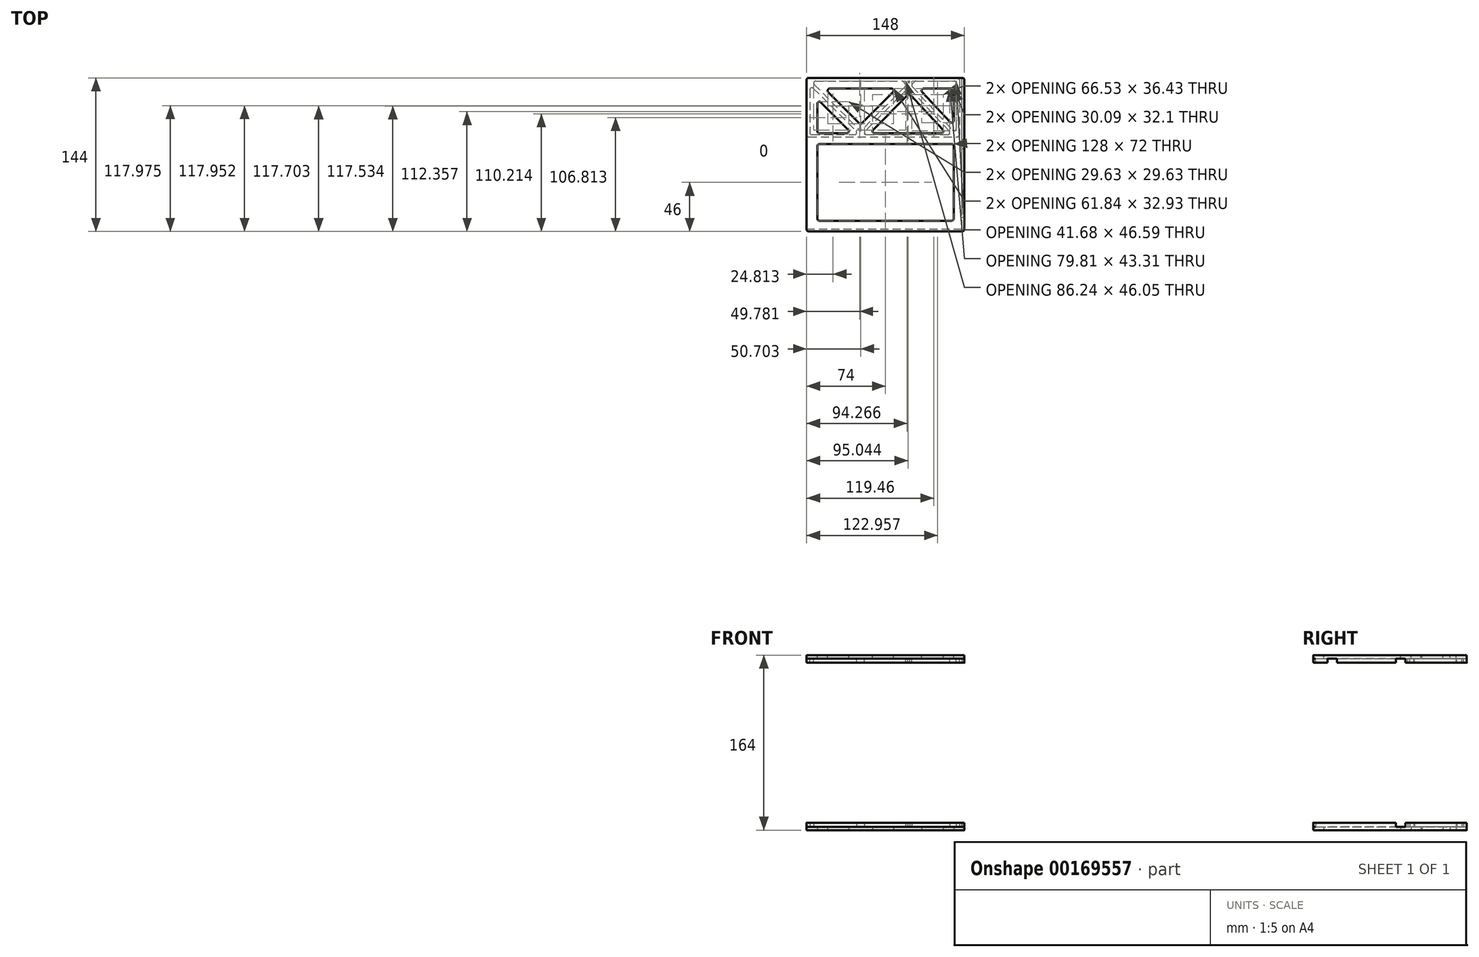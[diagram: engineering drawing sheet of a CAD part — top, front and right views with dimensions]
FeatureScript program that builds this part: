
annotation { "Feature Type Name" : "Feature", "Feature Type Description" : "" }
export const myFeature = defineFeature(function(context is Context, id is Id, definition is map)
    precondition{}
    {
        {
            var Q0;
            Q0=qCreatedBy(makeId("Top.planeOp"),FACE);
            var sketch = newSketch(context, id + "F0", { "sketchPlane" : qUnion([Q0])});
            skLineSegment(sketch, "E0.bottom", {"start": v(72, -72) * mm, "end": v(-72, -72) * mm});
            skLineSegment(sketch, "E0.top", {"start": v(72, 72) * mm, "end": v(-72, 72) * mm});
            skLineSegment(sketch, "E0.left", {"start": v(74, -70) * mm, "end": v(74, 70) * mm});
            skLineSegment(sketch, "E0.right", {"start": v(-74, -70) * mm, "end": v(-74, 70) * mm});
            skPoint(sketch, "E0.middle", {"position": v(0, 0) * mm});
            skLineSegment(sketch, "E1", {"start": v(-64, 8) * mm, "end": v(-64, -60) * mm});
            skLineSegment(sketch, "E2", {"start": v(-62, 20) * mm, "end": v(-36.36, 20) * mm});
            skPoint(sketch, "E3.end.orphan", {"position": v(-74, 0) * mm});
            skLineSegment(sketch, "E4", {"start": v(64, 60) * mm, "end": v(64, 31.9) * mm});
            skLineSegment(sketch, "E5", {"start": v(-71, -69) * mm, "end": v(71, -69) * mm, "construction": true});
            skLineSegment(sketch, "E6", {"start": v(71, -69) * mm, "end": v(71, 68) * mm, "construction": true});
            skLineSegment(sketch, "E7", {"start": v(71, 68) * mm, "end": v(69, 68) * mm, "construction": true});
            skLineSegment(sketch, "E8", {"start": v(69, 68) * mm, "end": v(69, 17) * mm, "construction": true});
            skLineSegment(sketch, "E9", {"start": v(69, 17) * mm, "end": v(-71, 17) * mm, "construction": true});
            skLineSegment(sketch, "E10", {"start": v(-71, 17) * mm, "end": v(-71, -69) * mm, "construction": true});
            skLineSegment(sketch, "E11.trimOffspring", {"start": v(-62, 10) * mm, "end": v(62, 10) * mm});
            skLineSegment(sketch, "E12.trimOffspring", {"start": v(64, 8) * mm, "end": v(64, -60) * mm});
            skLineSegment(sketch, "E13.trimOffspring", {"start": v(-62, -62) * mm, "end": v(62, -62) * mm});
            skLineSegment(sketch, "E14", {"start": v(-60.59, 49.05) * mm, "end": v(-34.95, 23.41) * mm});
            skLineSegment(sketch, "E15", {"start": v(-11.64, 23.41) * mm, "end": v(20.79, 55.84) * mm});
            skLineSegment(sketch, "E16", {"start": v(18.94, 62) * mm, "end": v(19.15, 62) * mm});
            skLineSegment(sketch, "E17", {"start": v(23.67, 55.8) * mm, "end": v(53.79, 23.36) * mm});
            skLineSegment(sketch, "E18", {"start": v(56.9, 20) * mm, "end": v(56.9, 20) * mm});
            skLineSegment(sketch, "E19", {"start": v(-53.64, 58.59) * mm, "end": v(-24.71, 29.65) * mm});
            skLineSegment(sketch, "E20", {"start": v(-21.88, 29.65) * mm, "end": v(7.05, 58.59) * mm});
            skLineSegment(sketch, "E21", {"start": v(34.43, 58.64) * mm, "end": v(60.53, 30.54) * mm});
            skLineSegment(sketch, "E22.trimOffspring", {"start": v(-10.23, 20) * mm, "end": v(52.32, 20) * mm});
            skPoint(sketch, "E23.visualSharp", {"position": v(-74, 72) * mm});
            skArc(sketch, "E23.filletArc", {"start": v(-72, 72) * mm, "mid": v(-73.41, 71.41) * mm, "end": v(-74, 70) * mm});
            skPoint(sketch, "E24.visualSharp", {"position": v(74, 72) * mm});
            skArc(sketch, "E24.filletArc", {"start": v(74, 70) * mm, "mid": v(73.41, 71.41) * mm, "end": v(72, 72) * mm});
            skLineSegment(sketch, "E25.trimOffspring", {"start": v(35.9, 62) * mm, "end": v(62, 62) * mm});
            skLineSegment(sketch, "E26.trimOffspring", {"start": v(-52.23, 62) * mm, "end": v(5.64, 62) * mm});
            skLineSegment(sketch, "E27.trimOffspring", {"start": v(-64, 22) * mm, "end": v(-64, 47.64) * mm});
            skPoint(sketch, "E28.visualSharp", {"position": v(-74, -72) * mm});
            skArc(sketch, "E28.filletArc", {"start": v(-74, -70) * mm, "mid": v(-73.41, -71.41) * mm, "end": v(-72, -72) * mm});
            skPoint(sketch, "E29.visualSharp", {"position": v(-64, -62) * mm});
            skArc(sketch, "E29.filletArc", {"start": v(-64, -60) * mm, "mid": v(-63.41, -61.41) * mm, "end": v(-62, -62) * mm});
            skPoint(sketch, "E30.visualSharp", {"position": v(64, -62) * mm});
            skArc(sketch, "E30.filletArc", {"start": v(62, -62) * mm, "mid": v(63.41, -61.41) * mm, "end": v(64, -60) * mm});
            skPoint(sketch, "E31.visualSharp", {"position": v(74, -72) * mm});
            skArc(sketch, "E31.filletArc", {"start": v(72, -72) * mm, "mid": v(73.41, -71.41) * mm, "end": v(74, -70) * mm});
            skPoint(sketch, "E32.visualSharp", {"position": v(64, 26.8) * mm});
            skArc(sketch, "E32.filletArc", {"start": v(60.53, 30.54) * mm, "mid": v(62.73, 30.04) * mm, "end": v(64, 31.9) * mm});
            skPoint(sketch, "E33.visualSharp", {"position": v(56.9, 20) * mm});
            skArc(sketch, "E33.filletArc", {"start": v(52.32, 20) * mm, "mid": v(54.15, 21.2) * mm, "end": v(53.79, 23.36) * mm});
            skPoint(sketch, "E34.visualSharp", {"position": v(64, 10) * mm});
            skArc(sketch, "E34.filletArc", {"start": v(64, 8) * mm, "mid": v(63.41, 9.41) * mm, "end": v(62, 10) * mm});
            skPoint(sketch, "E35.visualSharp", {"position": v(-23.3, 28.24) * mm});
            skArc(sketch, "E35.filletArc", {"start": v(-24.71, 29.65) * mm, "mid": v(-23.3, 29.07) * mm, "end": v(-21.88, 29.65) * mm});
            skPoint(sketch, "E36.visualSharp", {"position": v(-15.06, 20) * mm});
            skArc(sketch, "E36.filletArc", {"start": v(-11.64, 23.41) * mm, "mid": v(-12.08, 21.23) * mm, "end": v(-10.23, 20) * mm});
            skPoint(sketch, "E37.visualSharp", {"position": v(-31.54, 20) * mm});
            skArc(sketch, "E37.filletArc", {"start": v(-36.36, 20) * mm, "mid": v(-34.52, 21.23) * mm, "end": v(-34.95, 23.41) * mm});
            skPoint(sketch, "E38.visualSharp", {"position": v(-64, 20) * mm});
            skArc(sketch, "E38.filletArc", {"start": v(-64, 22) * mm, "mid": v(-63.41, 20.59) * mm, "end": v(-62, 20) * mm});
            skPoint(sketch, "E39.visualSharp", {"position": v(-64, 10) * mm});
            skArc(sketch, "E39.filletArc", {"start": v(-62, 10) * mm, "mid": v(-63.41, 9.41) * mm, "end": v(-64, 8) * mm});
            skPoint(sketch, "E40.visualSharp", {"position": v(-64, 52.46) * mm});
            skArc(sketch, "E40.filletArc", {"start": v(-60.59, 49.05) * mm, "mid": v(-62.77, 49.48) * mm, "end": v(-64, 47.64) * mm});
            skPoint(sketch, "E41.visualSharp", {"position": v(-57.06, 62) * mm});
            skArc(sketch, "E41.filletArc", {"start": v(-52.23, 62) * mm, "mid": v(-54.08, 60.77) * mm, "end": v(-53.64, 58.59) * mm});
            skPoint(sketch, "E42.visualSharp", {"position": v(10.46, 62) * mm});
            skArc(sketch, "E42.filletArc", {"start": v(7.05, 58.59) * mm, "mid": v(7.48, 60.77) * mm, "end": v(5.64, 62) * mm});
            skArc(sketch, "E43.filletArc", {"start": v(23.67, 55.8) * mm, "mid": v(22.24, 56.43) * mm, "end": v(20.79, 55.84) * mm});
            skPoint(sketch, "E44.visualSharp", {"position": v(31.31, 62) * mm});
            skArc(sketch, "E44.filletArc", {"start": v(35.9, 62) * mm, "mid": v(34.07, 60.8) * mm, "end": v(34.43, 58.64) * mm});
            skPoint(sketch, "E45.visualSharp", {"position": v(64, 62) * mm});
            skArc(sketch, "E45.filletArc", {"start": v(64, 60) * mm, "mid": v(63.41, 61.41) * mm, "end": v(62, 62) * mm});
            skSolve(sketch);
        }
        {
            var Q0;
            Q0 = qSketchRegion(id + "F0", true);
            var Q1;
            {var subQ0=sQuery(id+"F0.wireOp",EDGE,"E14");Q1=makeQuery(id+"F0.imprint","IMPRINT",FACE,{"disambiguationData":[TD([[makeQuery(id+"F0.imprint","IMPRINT",EDGE,{"derivedFrom":subQ0}),1.0]])]});}
            extrude(context, id + "F1", {"entities" : qUnion([Q0, Q1]), "depth" : 3 * mm});
        }
        {
            var Q0;
            Q0=makeQuery(id+"F1.opExtrude","CAP_FACE",FACE,{"disambiguationData":[OSD([sQuery(id+"F0.wireOp",EDGE,"E0.bottom"),sQuery(id+"F0.wireOp",EDGE,"E0.top"),sQuery(id+"F0.wireOp",EDGE,"E0.left"),sQuery(id+"F0.wireOp",EDGE,"E0.right"),sQuery(id+"F0.wireOp",EDGE,"E1"),sQuery(id+"F0.wireOp",EDGE,"E2"),sQuery(id+"F0.wireOp",EDGE,"E4"),sQuery(id+"F0.wireOp",EDGE,"E11.trimOffspring"),sQuery(id+"F0.wireOp",EDGE,"E12.trimOffspring"),sQuery(id+"F0.wireOp",EDGE,"E13.trimOffspring"),sQuery(id+"F0.wireOp",EDGE,"E14"),sQuery(id+"F0.wireOp",EDGE,"E15"),sQuery(id+"F0.wireOp",EDGE,"E17"),sQuery(id+"F0.wireOp",EDGE,"E19"),sQuery(id+"F0.wireOp",EDGE,"E20"),sQuery(id+"F0.wireOp",EDGE,"E21"),sQuery(id+"F0.wireOp",EDGE,"E22.trimOffspring"),sQuery(id+"F0.wireOp",EDGE,"E23.filletArc"),sQuery(id+"F0.wireOp",EDGE,"E24.filletArc"),sQuery(id+"F0.wireOp",EDGE,"E25.trimOffspring"),sQuery(id+"F0.wireOp",EDGE,"E26.trimOffspring"),sQuery(id+"F0.wireOp",EDGE,"E27.trimOffspring"),sQuery(id+"F0.wireOp",EDGE,"E28.filletArc"),sQuery(id+"F0.wireOp",EDGE,"E29.filletArc"),sQuery(id+"F0.wireOp",EDGE,"E30.filletArc"),sQuery(id+"F0.wireOp",EDGE,"E31.filletArc"),sQuery(id+"F0.wireOp",EDGE,"E32.filletArc"),sQuery(id+"F0.wireOp",EDGE,"E33.filletArc"),sQuery(id+"F0.wireOp",EDGE,"E34.filletArc"),sQuery(id+"F0.wireOp",EDGE,"E35.filletArc"),sQuery(id+"F0.wireOp",EDGE,"E36.filletArc"),sQuery(id+"F0.wireOp",EDGE,"E37.filletArc"),sQuery(id+"F0.wireOp",EDGE,"E38.filletArc"),sQuery(id+"F0.wireOp",EDGE,"E39.filletArc"),sQuery(id+"F0.wireOp",EDGE,"E40.filletArc"),sQuery(id+"F0.wireOp",EDGE,"E41.filletArc"),sQuery(id+"F0.wireOp",EDGE,"E42.filletArc"),sQuery(id+"F0.wireOp",EDGE,"E43.filletArc"),sQuery(id+"F0.wireOp",EDGE,"E44.filletArc"),sQuery(id+"F0.wireOp",EDGE,"E45.filletArc")])],"isStart":false});
            var sketch = newSketch(context, id + "F2", { "sketchPlane" : qUnion([Q0])});
            skLineSegment(sketch, "E46", {"start": v(-70.5, -69.5) * mm, "end": v(71.5, -69.5) * mm, "construction": true});
            skLineSegment(sketch, "E47", {"start": v(71.5, -69.5) * mm, "end": v(71.5, 67.5) * mm, "construction": true});
            skLineSegment(sketch, "E48", {"start": v(69.5, 67.5) * mm, "end": v(69.5, 16.5) * mm, "construction": true});
            skLineSegment(sketch, "E49", {"start": v(-70.5, -69.5) * mm, "end": v(-70.5, 16.5) * mm, "construction": true});
            skLineSegment(sketch, "E50", {"start": v(-70.5, 16.5) * mm, "end": v(69.5, 16.5) * mm, "construction": true});
            skLineSegment(sketch, "E51", {"start": v(69.5, 67.5) * mm, "end": v(71.5, 67.5) * mm, "construction": true});
            skPoint(sketch, "E52.orphan", {"position": v(69.5, 62) * mm});
            skLineSegment(sketch, "E53", {"start": v(-73.8, -69.7) * mm, "end": v(70.7, -69.7) * mm});
            skLineSegment(sketch, "E54", {"start": v(-74, -69.99) * mm, "end": v(-74, -69.9) * mm});
            skLineSegment(sketch, "E55", {"start": v(-72, -71.99) * mm, "end": v(72, -71.99) * mm});
            skPoint(sketch, "E56.orphan", {"position": v(74, -78.34) * mm});
            skLineSegment(sketch, "E57", {"start": v(74, -69.7) * mm, "end": v(74, -72) * mm});
            skPoint(sketch, "E58.endSnap0", {"position": v(0, -72) * mm});
            skPoint(sketch, "E59.orphan", {"position": v(74, 79.85) * mm});
            skPoint(sketch, "E60.orphan", {"position": v(83.1, -72) * mm});
            skPoint(sketch, "E58.start.orphan", {"position": v(-88.71, -71.99) * mm});
            skLineSegment(sketch, "E61", {"start": v(-72, 72) * mm, "end": v(67.3, 72) * mm});
            skLineSegment(sketch, "E62", {"start": v(74, 70) * mm, "end": v(74, 20) * mm});
            skPoint(sketch, "E63.orphan", {"position": v(-80.12, 72) * mm});
            skPoint(sketch, "E64.orphan", {"position": v(74, 76.3) * mm});
            skPoint(sketch, "E65.visualSharp", {"position": v(-74, 72) * mm});
            skArc(sketch, "E65.filletArc", {"start": v(-72, 72) * mm, "mid": v(-73.41, 71.41) * mm, "end": v(-74, 70) * mm});
            skPoint(sketch, "E66.visualSharp", {"position": v(74, 72) * mm});
            skArc(sketch, "E66.filletArc", {"start": v(74, 70) * mm, "mid": v(73.5, 71.31) * mm, "end": v(72.28, 71.98) * mm});
            skArc(sketch, "E67.filletArc", {"start": v(72, -71.99) * mm, "mid": v(73.41, -71.4) * mm, "end": v(74, -69.99) * mm});
            skPoint(sketch, "E68.visualSharp", {"position": v(-74, -71.99) * mm});
            skArc(sketch, "E68.filletArc", {"start": v(-74, -69.99) * mm, "mid": v(-73.41, -71.4) * mm, "end": v(-72, -71.99) * mm});
            skLineSegment(sketch, "E69", {"start": v(71.7, -72) * mm, "end": v(71.7, -71.99) * mm});
            skLineSegment(sketch, "E70.trimOffspring", {"start": v(71.7, -68.7) * mm, "end": v(71.7, 71.48) * mm});
            skPoint(sketch, "E71.visualSharp", {"position": v(71.7, -69.7) * mm});
            skArc(sketch, "E71.filletArc", {"start": v(70.7, -69.7) * mm, "mid": v(71.4, -69.4) * mm, "end": v(71.7, -68.7) * mm});
            skLineSegment(sketch, "E72", {"start": v(-72, 16.7) * mm, "end": v(67.3, 16.7) * mm});
            skLineSegment(sketch, "E73.trimOffspring", {"start": v(74, 16.7) * mm, "end": v(74, -69.99) * mm});
            skPoint(sketch, "E74.trimOffspring.end.orphan", {"position": v(-78.1, 20) * mm});
            skLineSegment(sketch, "E75", {"start": v(-69, 18.7) * mm, "end": v(-28.95, 18.7) * mm});
            skLineSegment(sketch, "E76", {"start": v(74, 22.4) * mm, "end": v(74, 11.64) * mm});
            skLineSegment(sketch, "E77", {"start": v(-71, 60.75) * mm, "end": v(-71, 20.7) * mm});
            skArc(sketch, "E78.filletArc", {"start": v(-71, 20.7) * mm, "mid": v(-70.41, 19.29) * mm, "end": v(-69, 18.7) * mm});
            skLineSegment(sketch, "E79", {"start": v(-65.35, 69) * mm, "end": v(15.18, 69) * mm});
            skLineSegment(sketch, "E80", {"start": v(-67.59, 62.17) * mm, "end": v(-27.53, 22.11) * mm});
            skLineSegment(sketch, "E81", {"start": v(-66.76, 65.59) * mm, "end": v(-24.71, 23.54) * mm});
            skLineSegment(sketch, "E82", {"start": v(27.24, 68.41) * mm, "end": v(25.2, 66.38) * mm});
            skLineSegment(sketch, "E83", {"start": v(22.79, 68.2) * mm, "end": v(22.14, 67.56) * mm});
            skLineSegment(sketch, "E84", {"start": v(16.64, 68.36) * mm, "end": v(18.37, 66.5) * mm});
            skLineSegment(sketch, "E85", {"start": v(20.87, 68.22) * mm, "end": v(21.47, 67.57) * mm});
            skArc(sketch, "E86.filletArc", {"start": v(-67.59, 62.17) * mm, "mid": v(-69.77, 62.6) * mm, "end": v(-71, 60.75) * mm});
            skPoint(sketch, "E87.newPointB", {"position": v(-79.62, 69) * mm});
            skArc(sketch, "E87.filletArc", {"start": v(-65.35, 69) * mm, "mid": v(-67.2, 67.77) * mm, "end": v(-66.76, 65.59) * mm});
            skLineSegment(sketch, "E88.trimOffspring", {"start": v(-17.65, 18.7) * mm, "end": v(58.18, 18.7) * mm});
            skPoint(sketch, "E89.visualSharp", {"position": v(-24.12, 18.7) * mm});
            skArc(sketch, "E89.filletArc", {"start": v(-28.95, 18.7) * mm, "mid": v(-27.1, 19.93) * mm, "end": v(-27.53, 22.11) * mm});
            skPoint(sketch, "E90.visualSharp", {"position": v(-22.47, 18.7) * mm});
            skArc(sketch, "E90.filletArc", {"start": v(-19.06, 22.11) * mm, "mid": v(-19.5, 19.93) * mm, "end": v(-17.65, 18.7) * mm});
            skArc(sketch, "E91.filletArc", {"start": v(-24.71, 23.54) * mm, "mid": v(-23.3, 22.95) * mm, "end": v(-21.88, 23.54) * mm});
            skLineSegment(sketch, "E92.trimOffspring", {"start": v(18.31, 63.73) * mm, "end": v(-21.88, 23.54) * mm});
            skLineSegment(sketch, "E93.trimOffspring", {"start": v(23.13, 61.37) * mm, "end": v(59.65, 22.06) * mm});
            skLineSegment(sketch, "E94.trimOffspring", {"start": v(25.15, 63.6) * mm, "end": v(62.83, 23.04) * mm});
            skLineSegment(sketch, "E95.trimOffspring", {"start": v(20.25, 61.43) * mm, "end": v(-19.06, 22.11) * mm});
            skLineSegment(sketch, "E96.trimOffspring", {"start": v(21.21, 69) * mm, "end": v(22.46, 69) * mm});
            skLineSegment(sketch, "E97.trimOffspring", {"start": v(28.65, 69) * mm, "end": v(64.3, 69) * mm});
            skPoint(sketch, "E98.visualSharp", {"position": v(16.05, 69) * mm});
            skArc(sketch, "E98.filletArc", {"start": v(16.64, 68.36) * mm, "mid": v(15.98, 68.83) * mm, "end": v(15.18, 69) * mm});
            skPoint(sketch, "E99.visualSharp", {"position": v(19.68, 65.1) * mm});
            skArc(sketch, "E99.filletArc", {"start": v(18.31, 63.73) * mm, "mid": v(18.9, 65.1) * mm, "end": v(18.37, 66.5) * mm});
            skPoint(sketch, "E100.visualSharp", {"position": v(20.14, 69) * mm});
            skArc(sketch, "E100.filletArc", {"start": v(21.21, 69) * mm, "mid": v(20.78, 68.72) * mm, "end": v(20.87, 68.22) * mm});
            skPoint(sketch, "E101.visualSharp", {"position": v(23.58, 69) * mm});
            skArc(sketch, "E101.filletArc", {"start": v(22.79, 68.2) * mm, "mid": v(22.89, 68.71) * mm, "end": v(22.46, 69) * mm});
            skPoint(sketch, "E102.visualSharp", {"position": v(21.8, 67.22) * mm});
            skArc(sketch, "E102.filletArc", {"start": v(21.47, 67.57) * mm, "mid": v(21.8, 67.42) * mm, "end": v(22.14, 67.56) * mm});
            skPoint(sketch, "E103.visualSharp", {"position": v(21.72, 62.9) * mm});
            skArc(sketch, "E103.filletArc", {"start": v(23.13, 61.37) * mm, "mid": v(21.7, 62.01) * mm, "end": v(20.25, 61.43) * mm});
            skPoint(sketch, "E104.visualSharp", {"position": v(23.84, 65.02) * mm});
            skArc(sketch, "E104.filletArc", {"start": v(25.2, 66.38) * mm, "mid": v(24.62, 65) * mm, "end": v(25.15, 63.6) * mm});
            skPoint(sketch, "E105.visualSharp", {"position": v(27.83, 69) * mm});
            skArc(sketch, "E105.filletArc", {"start": v(28.65, 69) * mm, "mid": v(27.89, 68.85) * mm, "end": v(27.24, 68.41) * mm});
            skPoint(sketch, "E106.visualSharp", {"position": v(62.77, 18.7) * mm});
            skArc(sketch, "E106.filletArc", {"start": v(58.18, 18.7) * mm, "mid": v(60.02, 19.9) * mm, "end": v(59.65, 22.06) * mm});
            skPoint(sketch, "E107.visualSharp", {"position": v(66.86, 18.7) * mm});
            skLineSegment(sketch, "E108", {"start": v(69.3, 70) * mm, "end": v(69.3, 18.7) * mm});
            skLineSegment(sketch, "E109", {"start": v(66.3, 73.83) * mm, "end": v(66.3, 72) * mm});
            skLineSegment(sketch, "E110.trimOffspring", {"start": v(66.3, 67) * mm, "end": v(66.3, 24.4) * mm});
            skPoint(sketch, "E111.trimOffspring.end.orphan", {"position": v(135.27, 69) * mm});
            skPoint(sketch, "E112.visualSharp", {"position": v(66.3, 69) * mm});
            skArc(sketch, "E112.filletArc", {"start": v(66.3, 67) * mm, "mid": v(65.71, 68.41) * mm, "end": v(64.3, 69) * mm});
            skLineSegment(sketch, "E113.trimOffspring", {"start": v(71.7, 72) * mm, "end": v(72, 72) * mm});
            skArc(sketch, "E114.filletArc", {"start": v(69.3, 70) * mm, "mid": v(68.71, 71.41) * mm, "end": v(67.3, 72) * mm});
            skArc(sketch, "E115.filletArc", {"start": v(72.28, 71.98) * mm, "mid": v(71.87, 71.86) * mm, "end": v(71.7, 71.48) * mm});
            skArc(sketch, "E116.filletArc", {"start": v(62.83, 23.04) * mm, "mid": v(65.03, 22.54) * mm, "end": v(66.3, 24.4) * mm});
            skArc(sketch, "E117.filletArc", {"start": v(67.3, 16.7) * mm, "mid": v(68.71, 17.29) * mm, "end": v(69.3, 18.7) * mm});
            skLineSegment(sketch, "E118", {"start": v(-74, 18.7) * mm, "end": v(-74, 70) * mm});
            skPoint(sketch, "E119.visualSharp", {"position": v(-74, 16.7) * mm});
            skArc(sketch, "E119.filletArc", {"start": v(-74, 18.7) * mm, "mid": v(-73.41, 17.29) * mm, "end": v(-72, 16.7) * mm});
            skLineSegment(sketch, "E120", {"start": v(-74, -69.7) * mm, "end": v(-74, 16.7) * mm});
            skPoint(sketch, "E121.visualSharp", {"position": v(-74, -69.7) * mm});
            skArc(sketch, "E121.filletArc", {"start": v(-73.8, -69.7) * mm, "mid": v(-73.94, -69.76) * mm, "end": v(-74, -69.9) * mm});
            skSolve(sketch);
        }
        {
            var Q0;
            Q0 = qSketchRegion(id + "F2", true);
            extrude(context, id + "F3", {"entities" : qUnion([Q0]), "operationType" : NewBodyOperationType.ADD, "depth" : 4 * mm});
        }
        {
            var Q0;
            Q0=makeQuery(id+"F1.opExtrude","SWEPT_BODY",BODY,{"disambiguationData":[OSD([sQuery(id+"F0.wireOp",EDGE,"E0.bottom"),sQuery(id+"F0.wireOp",EDGE,"E0.top"),sQuery(id+"F0.wireOp",EDGE,"E0.left"),sQuery(id+"F0.wireOp",EDGE,"E0.right"),sQuery(id+"F0.wireOp",EDGE,"E1"),sQuery(id+"F0.wireOp",EDGE,"E2"),sQuery(id+"F0.wireOp",EDGE,"E4"),sQuery(id+"F0.wireOp",EDGE,"E11.trimOffspring"),sQuery(id+"F0.wireOp",EDGE,"E12.trimOffspring"),sQuery(id+"F0.wireOp",EDGE,"E13.trimOffspring"),sQuery(id+"F0.wireOp",EDGE,"E14"),sQuery(id+"F0.wireOp",EDGE,"E15"),sQuery(id+"F0.wireOp",EDGE,"E17"),sQuery(id+"F0.wireOp",EDGE,"E19"),sQuery(id+"F0.wireOp",EDGE,"E20"),sQuery(id+"F0.wireOp",EDGE,"E21"),sQuery(id+"F0.wireOp",EDGE,"E22.trimOffspring"),sQuery(id+"F0.wireOp",EDGE,"E23.filletArc"),sQuery(id+"F0.wireOp",EDGE,"E24.filletArc"),sQuery(id+"F0.wireOp",EDGE,"E25.trimOffspring"),sQuery(id+"F0.wireOp",EDGE,"E26.trimOffspring"),sQuery(id+"F0.wireOp",EDGE,"E27.trimOffspring"),sQuery(id+"F0.wireOp",EDGE,"E28.filletArc"),sQuery(id+"F0.wireOp",EDGE,"E29.filletArc"),sQuery(id+"F0.wireOp",EDGE,"E30.filletArc"),sQuery(id+"F0.wireOp",EDGE,"E31.filletArc"),sQuery(id+"F0.wireOp",EDGE,"E32.filletArc"),sQuery(id+"F0.wireOp",EDGE,"E33.filletArc"),sQuery(id+"F0.wireOp",EDGE,"E34.filletArc"),sQuery(id+"F0.wireOp",EDGE,"E35.filletArc"),sQuery(id+"F0.wireOp",EDGE,"E36.filletArc"),sQuery(id+"F0.wireOp",EDGE,"E37.filletArc"),sQuery(id+"F0.wireOp",EDGE,"E38.filletArc"),sQuery(id+"F0.wireOp",EDGE,"E39.filletArc"),sQuery(id+"F0.wireOp",EDGE,"E40.filletArc"),sQuery(id+"F0.wireOp",EDGE,"E41.filletArc"),sQuery(id+"F0.wireOp",EDGE,"E42.filletArc"),sQuery(id+"F0.wireOp",EDGE,"E43.filletArc"),sQuery(id+"F0.wireOp",EDGE,"E44.filletArc"),sQuery(id+"F0.wireOp",EDGE,"E45.filletArc")])]});
            var Q1;
            Q1=makeQuery(id+"F3.opExtrude","CAP_FACE",FACE,{"disambiguationData":[OSD([sQuery(id+"F2.wireOp",EDGE,"E61"),sQuery(id+"F2.wireOp",EDGE,"E65.filletArc"),sQuery(id+"F2.wireOp",EDGE,"E72"),sQuery(id+"F2.wireOp",EDGE,"E75"),sQuery(id+"F2.wireOp",EDGE,"E77"),sQuery(id+"F2.wireOp",EDGE,"E78.filletArc"),sQuery(id+"F2.wireOp",EDGE,"E79"),sQuery(id+"F2.wireOp",EDGE,"E80"),sQuery(id+"F2.wireOp",EDGE,"E81"),sQuery(id+"F2.wireOp",EDGE,"E82"),sQuery(id+"F2.wireOp",EDGE,"E83"),sQuery(id+"F2.wireOp",EDGE,"E84"),sQuery(id+"F2.wireOp",EDGE,"E85"),sQuery(id+"F2.wireOp",EDGE,"E86.filletArc"),sQuery(id+"F2.wireOp",EDGE,"E87.filletArc"),sQuery(id+"F2.wireOp",EDGE,"E88.trimOffspring"),sQuery(id+"F2.wireOp",EDGE,"E89.filletArc"),sQuery(id+"F2.wireOp",EDGE,"E90.filletArc"),sQuery(id+"F2.wireOp",EDGE,"E91.filletArc"),sQuery(id+"F2.wireOp",EDGE,"E92.trimOffspring"),sQuery(id+"F2.wireOp",EDGE,"E93.trimOffspring"),sQuery(id+"F2.wireOp",EDGE,"E94.trimOffspring"),sQuery(id+"F2.wireOp",EDGE,"E95.trimOffspring"),sQuery(id+"F2.wireOp",EDGE,"E96.trimOffspring"),sQuery(id+"F2.wireOp",EDGE,"E97.trimOffspring"),sQuery(id+"F2.wireOp",EDGE,"E98.filletArc"),sQuery(id+"F2.wireOp",EDGE,"E99.filletArc"),sQuery(id+"F2.wireOp",EDGE,"E100.filletArc"),sQuery(id+"F2.wireOp",EDGE,"E101.filletArc"),sQuery(id+"F2.wireOp",EDGE,"E102.filletArc"),sQuery(id+"F2.wireOp",EDGE,"E103.filletArc"),sQuery(id+"F2.wireOp",EDGE,"E104.filletArc"),sQuery(id+"F2.wireOp",EDGE,"E105.filletArc"),sQuery(id+"F2.wireOp",EDGE,"E106.filletArc"),sQuery(id+"F2.wireOp",EDGE,"E108"),sQuery(id+"F2.wireOp",EDGE,"E110.trimOffspring"),sQuery(id+"F2.wireOp",EDGE,"E112.filletArc"),sQuery(id+"F2.wireOp",EDGE,"E114.filletArc"),sQuery(id+"F2.wireOp",EDGE,"E116.filletArc"),sQuery(id+"F2.wireOp",EDGE,"E117.filletArc"),sQuery(id+"F2.wireOp",EDGE,"E118"),sQuery(id+"F2.wireOp",EDGE,"E119.filletArc")])],"isStart":false});
            mirror(context, id + "F4", {"entities" : qUnion([Q0]), "mirrorPlane" : qUnion([Q1])});
        }
        {
            var Q0;
            Q0=makeQuery(id+"F4.opPattern","COPY",BODY,{"derivedFrom":makeQuery(id+"F1.opExtrude","SWEPT_BODY",BODY,{"disambiguationData":[OSD([sQuery(id+"F0.wireOp",EDGE,"E0.bottom"),sQuery(id+"F0.wireOp",EDGE,"E0.top"),sQuery(id+"F0.wireOp",EDGE,"E0.left"),sQuery(id+"F0.wireOp",EDGE,"E0.right"),sQuery(id+"F0.wireOp",EDGE,"E1"),sQuery(id+"F0.wireOp",EDGE,"E2"),sQuery(id+"F0.wireOp",EDGE,"E4"),sQuery(id+"F0.wireOp",EDGE,"E11.trimOffspring"),sQuery(id+"F0.wireOp",EDGE,"E12.trimOffspring"),sQuery(id+"F0.wireOp",EDGE,"E13.trimOffspring"),sQuery(id+"F0.wireOp",EDGE,"E14"),sQuery(id+"F0.wireOp",EDGE,"E15"),sQuery(id+"F0.wireOp",EDGE,"E17"),sQuery(id+"F0.wireOp",EDGE,"E19"),sQuery(id+"F0.wireOp",EDGE,"E20"),sQuery(id+"F0.wireOp",EDGE,"E21"),sQuery(id+"F0.wireOp",EDGE,"E22.trimOffspring"),sQuery(id+"F0.wireOp",EDGE,"E23.filletArc"),sQuery(id+"F0.wireOp",EDGE,"E24.filletArc"),sQuery(id+"F0.wireOp",EDGE,"E25.trimOffspring"),sQuery(id+"F0.wireOp",EDGE,"E26.trimOffspring"),sQuery(id+"F0.wireOp",EDGE,"E27.trimOffspring"),sQuery(id+"F0.wireOp",EDGE,"E28.filletArc"),sQuery(id+"F0.wireOp",EDGE,"E29.filletArc"),sQuery(id+"F0.wireOp",EDGE,"E30.filletArc"),sQuery(id+"F0.wireOp",EDGE,"E31.filletArc"),sQuery(id+"F0.wireOp",EDGE,"E32.filletArc"),sQuery(id+"F0.wireOp",EDGE,"E33.filletArc"),sQuery(id+"F0.wireOp",EDGE,"E34.filletArc"),sQuery(id+"F0.wireOp",EDGE,"E35.filletArc"),sQuery(id+"F0.wireOp",EDGE,"E36.filletArc"),sQuery(id+"F0.wireOp",EDGE,"E37.filletArc"),sQuery(id+"F0.wireOp",EDGE,"E38.filletArc"),sQuery(id+"F0.wireOp",EDGE,"E39.filletArc"),sQuery(id+"F0.wireOp",EDGE,"E40.filletArc"),sQuery(id+"F0.wireOp",EDGE,"E41.filletArc"),sQuery(id+"F0.wireOp",EDGE,"E42.filletArc"),sQuery(id+"F0.wireOp",EDGE,"E43.filletArc"),sQuery(id+"F0.wireOp",EDGE,"E44.filletArc"),sQuery(id+"F0.wireOp",EDGE,"E45.filletArc")])]}),"instanceName":"1"});
            transform(context, id + "F5", {"entities" : qUnion([Q0]), "transformType" : TransformType.TRANSLATION_3D, "dx" : 0 * mm, "dy" : 0 * mm, "dz" : 150 * mm, "makeCopy" : false});
        }
        {
            var Q0;
            Q0=makeQuery(id+"F4.opPattern","COPY",FACE,{"derivedFrom":makeQuery(id+"F3.boolean.opBoolean","MERGE",FACE,{"derivedFrom":[makeQuery(id+"F1.opExtrude","SWEPT_FACE",FACE,{"disambiguationData":[OSD([sQuery(id+"F0.wireOp",EDGE,"E0.left")])]}),makeQuery(id+"F3.opExtrude","SWEPT_FACE",FACE,{"disambiguationData":[OSD([sQuery(id+"F2.wireOp",EDGE,"E62"),sQuery(id+"F2.wireOp",EDGE,"E73.trimOffspring"),sQuery(id+"F2.wireOp",EDGE,"E76")])]})]}),"instanceName":"1"});
            var sketch = newSketch(context, id + "F6", { "sketchPlane" : qUnion([Q0])});
            skPoint(sketch, "E122", {"position": v(-53.99, 159) * mm});
            skLineSegment(sketch, "E123", {"start": v(-69.99, 161) * mm, "end": v(70, 161) * mm, "construction": true});
            skLineSegment(sketch, "E124.bottom", {"start": v(-49.49, 157) * mm, "end": v(-58.49, 157) * mm});
            skLineSegment(sketch, "E124.top", {"start": v(-49.49, 161) * mm, "end": v(-58.49, 161) * mm});
            skLineSegment(sketch, "E124.left", {"start": v(-49.49, 157) * mm, "end": v(-49.49, 161) * mm});
            skLineSegment(sketch, "E124.right", {"start": v(-58.49, 157) * mm, "end": v(-58.49, 161) * mm});
            skPoint(sketch, "E125", {"position": v(10.01, 158.98) * mm});
            skLineSegment(sketch, "E126.bottom", {"start": v(14.51, 156.98) * mm, "end": v(5.51, 156.98) * mm});
            skLineSegment(sketch, "E126.top", {"start": v(14.51, 160.98) * mm, "end": v(5.51, 160.98) * mm});
            skLineSegment(sketch, "E126.left", {"start": v(14.51, 156.98) * mm, "end": v(14.51, 160.98) * mm});
            skLineSegment(sketch, "E126.right", {"start": v(5.51, 156.98) * mm, "end": v(5.51, 160.98) * mm});
            skLineSegment(sketch, "E127", {"start": v(-69.85, 3.1) * mm, "end": v(69.98, 3.1) * mm, "construction": true});
            skLineSegment(sketch, "E128", {"start": v(10.01, 7.15) * mm, "end": v(10.01, 3.1) * mm, "construction": true});
            skLineSegment(sketch, "E129.bottom", {"start": v(14.51, 7.15) * mm, "end": v(5.51, 7.15) * mm});
            skLineSegment(sketch, "E129.top", {"start": v(14.51, 3.1) * mm, "end": v(5.51, 3.1) * mm});
            skLineSegment(sketch, "E129.left", {"start": v(14.51, 7.15) * mm, "end": v(14.51, 3.1) * mm});
            skLineSegment(sketch, "E129.right", {"start": v(5.51, 7.15) * mm, "end": v(5.51, 3.1) * mm});
            skPoint(sketch, "E129.middle", {"position": v(10.01, 5.13) * mm});
            skSolve(sketch);
        }
        {
            var Q0;
            Q0 = qSketchRegion(id + "F6", true);
            extrude(context, id + "F7", {"entities" : qUnion([Q0]), "operationType" : NewBodyOperationType.REMOVE, "oppositeDirection" : true, "depth" : 25 * mm});
        }
        {
            var Q0;
            Q0 = qSketchRegion(id + "F6", true);
            extrude(context, id + "F8", {"entities" : qUnion([Q0]), "operationType" : NewBodyOperationType.REMOVE, "oppositeDirection" : true, "depth" : 25 * mm});
        }
    });
